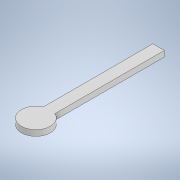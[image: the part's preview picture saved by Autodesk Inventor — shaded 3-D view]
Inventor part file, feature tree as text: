
AUTODESK INVENTOR PART (.ipt)
format: ipt  version: 2020 (Build 240168000, 168)  size: 103,936 bytes
history: native  units: in
note: dims shown in document units (in); Inventor stores cm internally (conversion verified against a paired STEP export)
features: sketch x4, extrude x2
ambient origin geometry x8: Origin, YZ Plane, XZ Plane, XY Plane, X Axis, Y Axis, Z Axis, Center Point
bodies: Solid1 (feature_tree)
feature tree (6):
  sketch  "Sketch1"  dims[d0=0.7874in d1=0.1575in d2=0.0in]
  sketch  "Sketch2"  dims[d3=0.1575in d4=0.315in]
  extrude  "Extrusion1"  Depth=0.1575in TaperAngle=0.0deg
  extrude  "Extrusion2"  Depth=0.315in
  sketch  "Sketch3"  dims[d5=0.315in]
  sketch  "Sketch4"  dims[d6=3.3465in d7=0.1575in d8=0.0in]
